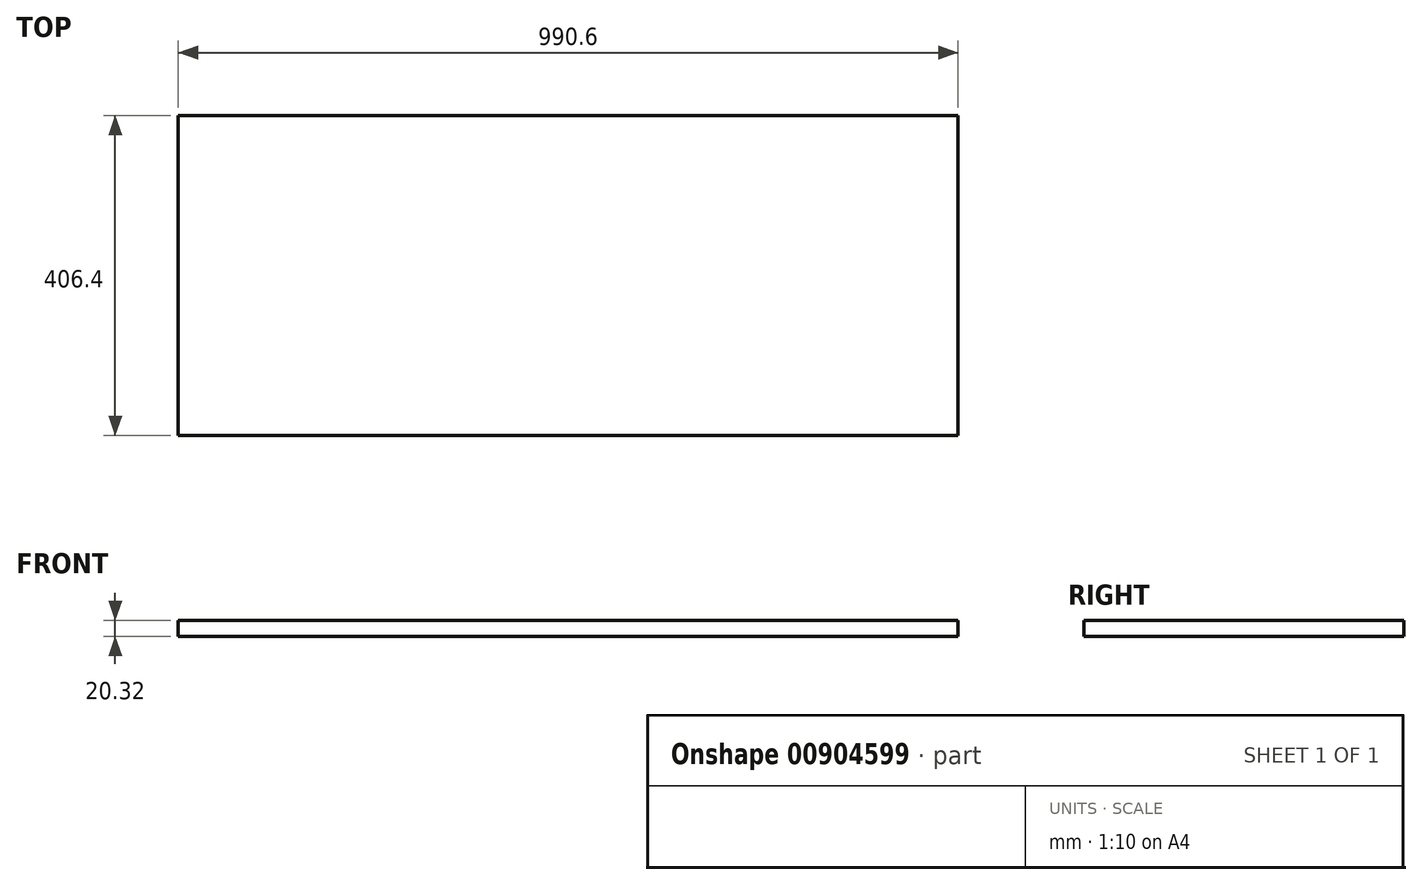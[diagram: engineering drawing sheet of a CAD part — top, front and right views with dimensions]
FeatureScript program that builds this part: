
annotation { "Feature Type Name" : "Feature", "Feature Type Description" : "" }
export const myFeature = defineFeature(function(context is Context, id is Id, definition is map)
    precondition{}
    {
        {
            var Q0;
            Q0=qCreatedBy(makeId("Top.planeOp"),FACE);
            var sketch = newSketch(context, id + "F0", { "sketchPlane" : qUnion([Q0])});
            skLineSegment(sketch, "E0.bottom", {"start": v(495.3, -203.2) * mm, "end": v(-495.3, -203.2) * mm});
            skLineSegment(sketch, "E0.top", {"start": v(495.3, 203.2) * mm, "end": v(-495.3, 203.2) * mm});
            skLineSegment(sketch, "E0.left", {"start": v(495.3, -203.2) * mm, "end": v(495.3, 203.2) * mm});
            skLineSegment(sketch, "E0.right", {"start": v(-495.3, -203.2) * mm, "end": v(-495.3, 203.2) * mm});
            skPoint(sketch, "E0.middle", {"position": v(0, 0) * mm});
            skSolve(sketch);
        }
        {
            var Q0;
            Q0=makeQuery(id+"F0.imprint","IMPRINT",FACE,{"disambiguationData":[TD([[makeQuery(id+"F0.imprint","IMPRINT",EDGE,{"derivedFrom":sQuery(id+"F0.wireOp",EDGE,"E0.bottom")}),-1.0]])]});
            extrude(context, id + "F1", {"entities" : qUnion([Q0]), "depth" : 20.32 * mm, "offsetDistance" : 25.4 * mm});
        }
    });
